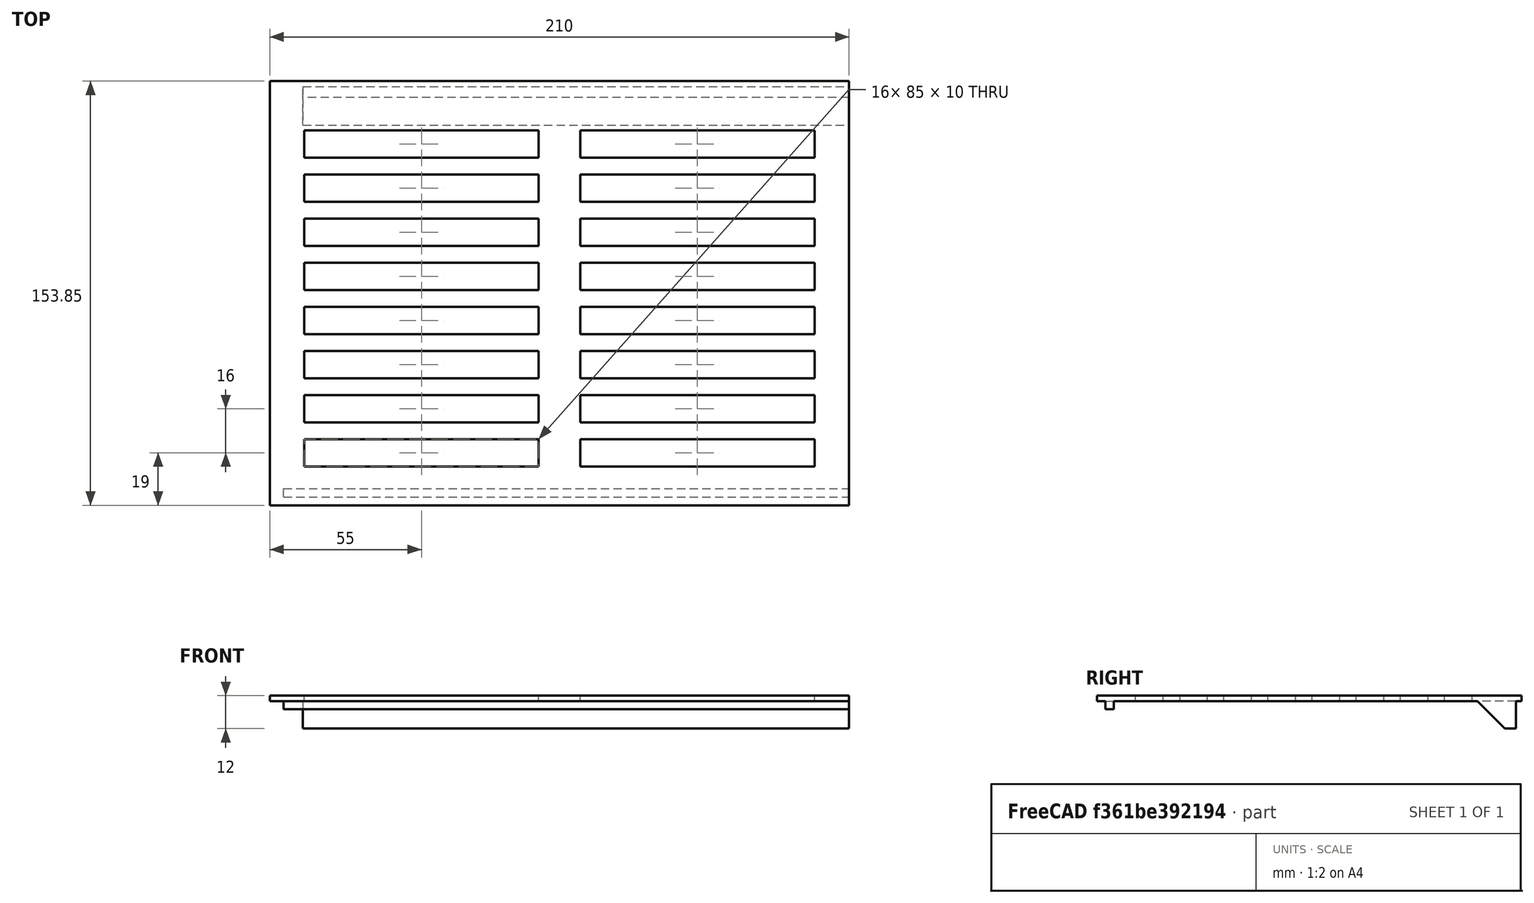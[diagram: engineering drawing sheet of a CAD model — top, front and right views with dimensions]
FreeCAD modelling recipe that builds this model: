
FCSTD DOCUMENT  (FreeCAD 0.17R13522 (Git))
Label: lateral_derecho
License: CreativeCommons Attribution-ShareAlike
LicenseURL: http://creativecommons.org/licenses/by-sa/4.0/
objects: Part::Box×7, Part::Cut×3, Part::Fuse×3, Part::FeaturePython×1
note: 14 computed .brp shape members not serialized (recipe doc carries the construction recipe); baked Part::Feature solids carry a one-line shape summary decoded from their .brp

FEATURE [Part::Box] Box  label="base lateral"
  AttacherType = Attacher::AttachEngine3D
  Height = 2
  Length = 210
  Width = 153.85
FEATURE [Part::Box] Box001  label="fleje arriba"
  AttacherType = Attacher::AttachEngine3D
  Height = 10
  Length = 198
  Placement = pos=(12,151.85,-10) rot=(0,0,1;0rad)
  Width = 4
FEATURE [Part::Box] Box002  label="fleje abajo"
  AttacherType = Attacher::AttachEngine3D
  Height = 3
  Length = 205
  Placement = pos=(5,3,-3) rot=(0,0,1;0rad)
  Width = 3
FEATURE [Part::Box] Box003  label="Cube"
  AttacherType = Attacher::AttachEngine3D
  Height = 14.14
  Length = 198
  Placement = pos=(0,100,40) rot=(1,0,0;0.785398rad)
  Width = 14.14
FEATURE [Part::Box] Box004  label="Cube001"
  AttacherType = Attacher::AttachEngine3D
  Height = 10
  Length = 220
  Placement = pos=(-6,76,40) rot=(0,0,1;0rad)
  Width = 36
FEATURE [Part::Box] Box005  label="Cube002"
  AttacherType = Attacher::AttachEngine3D
  Height = 27
  Length = 220
  Placement = pos=(-7,110,72) rot=(1,0,0;3.14159rad)
  Width = 10
FEATURE [Part::Cut] Cut
  Base = -> Box003
  Refine = true
  Tool = -> Box005
FEATURE [Part::Cut] Cut001
  Base = -> Cut
  Placement = pos=(210,51.85,50) rot=(0,1,0;3.14159rad)
  Refine = true
  Tool = -> Box004
FEATURE [Part::Fuse] Fusion
  Base = -> Box
  Refine = true
  Tool = -> Box002
FEATURE [Part::Fuse] Fusion002002  label="apoyo_para_techo_con_chaflan_10"
  Base = -> Box001
  Placement = pos=(0,-4,0) rot=(0,0,1;0rad)
  Refine = true
  Tool = -> Cut001
FEATURE [Part::Fuse] Fusion002003  label="lateral derecho"
  Base = -> Fusion
  Refine = true
  Tool = -> Fusion002002
FEATURE [Part::Box] Box006  label="Cube003"
  AttacherType = Attacher::AttachEngine3D
  Height = 10
  Length = 85
  Placement = pos=(12.5,14,0) rot=(0,0,1;0rad)
  Width = 10
FEATURE [Part::FeaturePython] Array  # Draft array (typed FeaturePython)
  Angle = 360
  ArrayType = 0
  Axis = (0,0,1)
  Base = -> Box006
  Center = (0,0,0)
  Fuse = false
  IntervalAxis = (0,0,0)
  IntervalX = (100,0,0)
  IntervalY = (0,16,0)
  IntervalZ = (0,0,0)
  NumberPolar = 1
  NumberX = 2
  NumberY = 8
  NumberZ = 1
  Placement = pos=(0,0,-4) rot=(0,0,1;0rad)
FEATURE [Part::Cut] Cut002
  Base = -> Fusion002003
  Refine = true
  Tool = -> Array
